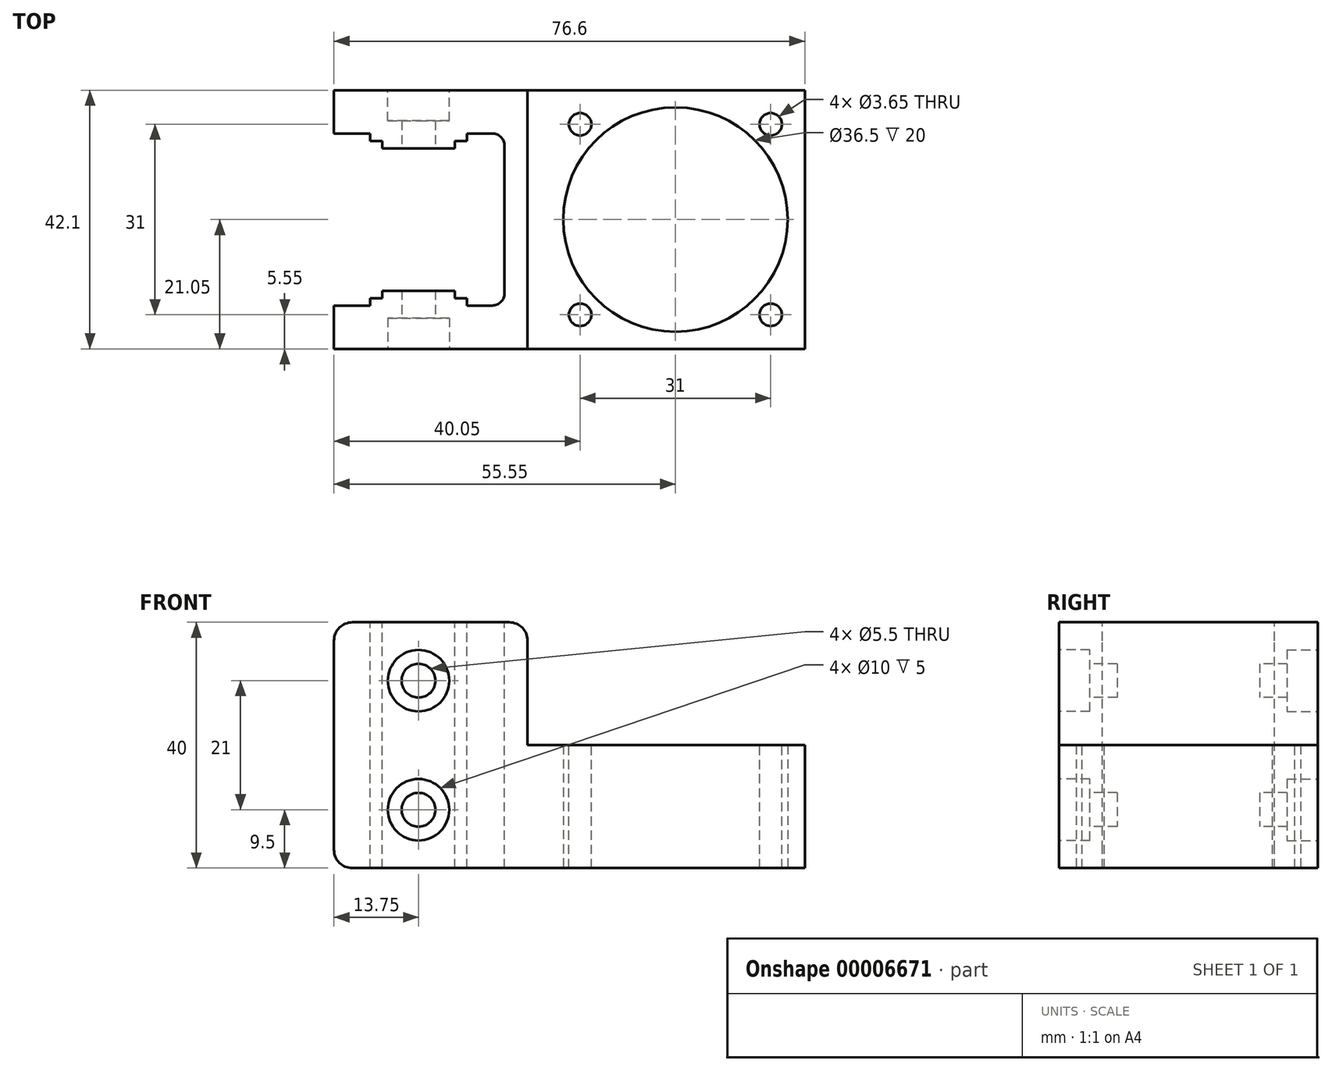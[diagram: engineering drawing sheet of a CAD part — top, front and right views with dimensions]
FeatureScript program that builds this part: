
annotation { "Feature Type Name" : "Feature", "Feature Type Description" : "" }
export const myFeature = defineFeature(function(context is Context, id is Id, definition is map)
    precondition{}
    {
        {
            var Q0;
            Q0=qCreatedBy(makeId("Top.planeOp"),FACE);
            var sketch = newSketch(context, id + "F0", { "sketchPlane" : qUnion([Q0])});
            skLineSegment(sketch, "E0.bottom", {"start": v(-34.5, 0) * mm, "end": v(42.1, 0) * mm});
            skLineSegment(sketch, "E0.top", {"start": v(-34.5, 42.1) * mm, "end": v(42.1, 42.1) * mm});
            skLineSegment(sketch, "E0.right", {"start": v(42.1, 0) * mm, "end": v(42.1, 42.1) * mm});
            skCircle(sketch, "E1", {"center": v(21.05, 21.05) * mm, "radius": 18.25 * mm});
            skLineSegment(sketch, "E2.0", {"start": v(-34.5, 0) * mm, "end": v(-34.5, 42.1) * mm});
            skSolve(sketch);
        }
        {
            var Q0;
            Q0 = qSketchRegion(id + "F0", true);
            extrude(context, id + "F1", {"entities" : qUnion([Q0]), "depth" : 20 * mm});
        }
        {
            var Q0;
            Q0=makeQuery(id+"F1.opExtrude","CAP_FACE",FACE,{"disambiguationData":[OSD([sQuery(id+"F0.wireOp",EDGE,"E0.bottom"),sQuery(id+"F0.wireOp",EDGE,"E0.top"),sQuery(id+"F0.wireOp",EDGE,"E0.right"),sQuery(id+"F0.wireOp",EDGE,"E1"),sQuery(id+"F0.wireOp",EDGE,"E2.0")])],"isStart":false});
            var sketch = newSketch(context, id + "F2", { "sketchPlane" : qUnion([Q0])});
            skLineSegment(sketch, "E3.0", {"start": v(21.05, 0) * mm, "end": v(21.05, 46.92) * mm, "construction": true});
            skLineSegment(sketch, "E4.0", {"start": v(0, 21.05) * mm, "end": v(47.18, 21.05) * mm, "construction": true});
            skLineSegment(sketch, "E5.0", {"start": v(36.55, 0) * mm, "end": v(36.55, 46.92) * mm, "construction": true});
            skLineSegment(sketch, "E6.0", {"start": v(5.55, 0) * mm, "end": v(5.55, 46.92) * mm, "construction": true});
            skLineSegment(sketch, "E7.0", {"start": v(0, 5.55) * mm, "end": v(47.18, 5.55) * mm, "construction": true});
            skLineSegment(sketch, "E8.0", {"start": v(0, 36.55) * mm, "end": v(47.18, 36.55) * mm, "construction": true});
            skCircle(sketch, "E9", {"center": v(5.55, 36.55) * mm, "radius": 1.82 * mm});
            skCircle(sketch, "E10", {"center": v(36.55, 36.55) * mm, "radius": 1.82 * mm});
            skCircle(sketch, "E11", {"center": v(36.55, 5.55) * mm, "radius": 1.82 * mm});
            skCircle(sketch, "E12", {"center": v(5.55, 5.55) * mm, "radius": 1.82 * mm});
            skSolve(sketch);
        }
        {
            var Q0;
            Q0 = qSketchRegion(id + "F2", true);
            extrude(context, id + "F3", {"entities" : qUnion([Q0]), "operationType" : NewBodyOperationType.REMOVE, "endBound" : BoundingType.THROUGH_ALL, "oppositeDirection" : true, "depth" : 25 * mm});
        }
        {
            var Q0;
            Q0=makeQuery(id+"F1.opExtrude","CAP_FACE",FACE,{"disambiguationData":[OSD([sQuery(id+"F0.wireOp",EDGE,"E0.bottom"),sQuery(id+"F0.wireOp",EDGE,"E0.top"),sQuery(id+"F0.wireOp",EDGE,"E0.right"),sQuery(id+"F0.wireOp",EDGE,"E1"),sQuery(id+"F0.wireOp",EDGE,"E2.0")])],"isStart":false});
            var sketch = newSketch(context, id + "F4", { "sketchPlane" : qUnion([Q0])});
            skLineSegment(sketch, "E13.bottom", {"start": v(-34.5, 42.1) * mm, "end": v(-3, 42.1) * mm});
            skLineSegment(sketch, "E13.top", {"start": v(-34.5, 0) * mm, "end": v(-3, 0) * mm});
            skLineSegment(sketch, "E13.left", {"start": v(-34.5, 42.1) * mm, "end": v(-34.5, 0) * mm});
            skLineSegment(sketch, "E13.right", {"start": v(-3, 42.1) * mm, "end": v(-3, 0) * mm});
            skSolve(sketch);
        }
        {
            var Q0;
            Q0 = qSketchRegion(id + "F4", true);
            extrude(context, id + "F5", {"entities" : qUnion([Q0]), "operationType" : NewBodyOperationType.ADD, "depth" : 20 * mm});
        }
        {
            var Q0;
            Q0=makeQuery(id+"F5.boolean.opBoolean","MERGE",FACE,{"derivedFrom":[makeQuery(id+"F1.opExtrude","SWEPT_FACE",FACE,{"disambiguationData":[OSD([sQuery(id+"F0.wireOp",EDGE,"E0.bottom")])]}),makeQuery(id+"F5.opExtrude","SWEPT_FACE",FACE,{"disambiguationData":[OSD([sQuery(id+"F4.wireOp",EDGE,"E13.top")])]})]});
            var sketch = newSketch(context, id + "F6", { "sketchPlane" : qUnion([Q0])});
            skLineSegment(sketch, "E14", {"start": v(-20.75, 40) * mm, "end": v(-20.75, 0) * mm, "construction": true});
            skLineSegment(sketch, "E15", {"start": v(-34.5, 0) * mm, "end": v(-10.11, 0) * mm, "construction": true});
            skLineSegment(sketch, "E16", {"start": v(-34.5, 40) * mm, "end": v(-8.27, 40) * mm, "construction": true});
            skLineSegment(sketch, "E17.0", {"start": v(-34.5, 30.5) * mm, "end": v(-8.27, 30.5) * mm, "construction": true});
            skLineSegment(sketch, "E18.0", {"start": v(-34.5, 9.5) * mm, "end": v(-10.11, 9.5) * mm, "construction": true});
            skCircle(sketch, "E19", {"center": v(-20.75, 30.5) * mm, "radius": 2.75 * mm});
            skCircle(sketch, "E20", {"center": v(-20.75, 9.5) * mm, "radius": 2.75 * mm});
            skSolve(sketch);
        }
        {
            var Q0;
            Q0 = qSketchRegion(id + "F6", true);
            extrude(context, id + "F7", {"entities" : qUnion([Q0]), "operationType" : NewBodyOperationType.REMOVE, "endBound" : BoundingType.THROUGH_ALL, "oppositeDirection" : true, "depth" : 25 * mm});
        }
        {
            var Q0;
            Q0=makeQuery(id+"F5.opExtrude","CAP_EDGE",EDGE,{"disambiguationData":[OSD([sQuery(id+"F4.wireOp",EDGE,"E13.left")])],"isStart":false});
            var Q1;
            Q1=makeQuery(id+"F5.opExtrude","CAP_EDGE",EDGE,{"disambiguationData":[OSD([sQuery(id+"F4.wireOp",EDGE,"E13.right")])],"isStart":false});
            var Q2;
            Q2=makeQuery(id+"F5.opExtrude","CAP_EDGE",EDGE,{"disambiguationData":[OSD([sQuery(id+"F4.wireOp",EDGE,"E13.right")])],"isStart":true});
            var Q3;
            Q3=makeQuery(id+"F1.opExtrude","CAP_EDGE",EDGE,{"disambiguationData":[OSD([sQuery(id+"F0.wireOp",EDGE,"E2.0")])],"isStart":true});
            fillet(context, id + "F8", {"entities" : qUnion([Q0, Q1, Q2, Q3]), "radius" : 3 * mm, "tangentPropagation" : true, "allowEdgeOverflow" : false});
        }
        {
            var Q0;
            Q0=makeQuery(id+"F5.boolean.opBoolean","MERGE",FACE,{"derivedFrom":[makeQuery(id+"F1.opExtrude","SWEPT_FACE",FACE,{"disambiguationData":[OSD([sQuery(id+"F0.wireOp",EDGE,"E0.bottom")])]}),makeQuery(id+"F5.opExtrude","SWEPT_FACE",FACE,{"disambiguationData":[OSD([sQuery(id+"F4.wireOp",EDGE,"E13.top")])]})]});
            var sketch = newSketch(context, id + "F9", { "sketchPlane" : qUnion([Q0])});
            skCircle(sketch, "E21", {"center": v(-20.75, 30.5) * mm, "radius": 5 * mm});
            skCircle(sketch, "E22", {"center": v(-20.75, 9.5) * mm, "radius": 5 * mm});
            skSolve(sketch);
        }
        {
            var Q0;
            Q0 = qSketchRegion(id + "F9", true);
            extrude(context, id + "F10", {"entities" : qUnion([Q0]), "operationType" : NewBodyOperationType.REMOVE, "oppositeDirection" : true, "depth" : 5 * mm});
        }
        {
            var Q0;
            Q0=makeQuery(id+"F5.boolean.opBoolean","MERGE",FACE,{"derivedFrom":[makeQuery(id+"F1.opExtrude","SWEPT_FACE",FACE,{"disambiguationData":[OSD([sQuery(id+"F0.wireOp",EDGE,"E0.top")])]}),makeQuery(id+"F5.opExtrude","SWEPT_FACE",FACE,{"disambiguationData":[OSD([sQuery(id+"F4.wireOp",EDGE,"E13.bottom")])]})]});
            var sketch = newSketch(context, id + "F11", { "sketchPlane" : qUnion([Q0])});
            skCircle(sketch, "E23", {"center": v(20.75, 30.5) * mm, "radius": 5 * mm});
            skCircle(sketch, "E24", {"center": v(20.75, 9.5) * mm, "radius": 5 * mm});
            skSolve(sketch);
        }
        {
            var Q0;
            Q0 = qSketchRegion(id + "F11", true);
            extrude(context, id + "F12", {"entities" : qUnion([Q0]), "operationType" : NewBodyOperationType.REMOVE, "oppositeDirection" : true, "depth" : 5 * mm});
        }
        {
            var Q0;
            Q0=makeQuery(id+"F5.opExtrude","CAP_FACE",FACE,{"disambiguationData":[OSD([sQuery(id+"F4.wireOp",EDGE,"E13.bottom"),sQuery(id+"F4.wireOp",EDGE,"E13.top"),sQuery(id+"F4.wireOp",EDGE,"E13.left"),sQuery(id+"F4.wireOp",EDGE,"E13.right")])],"isStart":false});
            var sketch = newSketch(context, id + "F13", { "sketchPlane" : qUnion([Q0])});
            skLineSegment(sketch, "E25.0", {"start": v(-14.85, 32.65) * mm, "end": v(-26.65, 32.65) * mm});
            skLineSegment(sketch, "E26.0", {"start": v(-26.65, 33.85) * mm, "end": v(-28.65, 33.85) * mm});
            skLineSegment(sketch, "E27.0", {"start": v(-12.85, 33.85) * mm, "end": v(-14.85, 33.85) * mm});
            skLineSegment(sketch, "E28.0", {"start": v(-8.75, 35.05) * mm, "end": v(-12.85, 35.05) * mm});
            skLineSegment(sketch, "E29.0", {"start": v(-28.65, 35.05) * mm, "end": v(-34.5, 35.05) * mm});
            skLineSegment(sketch, "E30.0", {"start": v(-28.65, 35.05) * mm, "end": v(-28.65, 33.85) * mm});
            skLineSegment(sketch, "E31.0", {"start": v(-26.65, 33.85) * mm, "end": v(-26.65, 32.65) * mm});
            skLineSegment(sketch, "E32.0", {"start": v(-14.85, 33.85) * mm, "end": v(-14.85, 32.65) * mm});
            skLineSegment(sketch, "E33.0", {"start": v(-12.85, 35.05) * mm, "end": v(-12.85, 33.85) * mm});
            skLineSegment(sketch, "E34.0", {"start": v(-6.75, 33.05) * mm, "end": v(-6.75, 9.05) * mm});
            skLineSegment(sketch, "E35.0", {"start": v(-28.65, 7.05) * mm, "end": v(-34.5, 7.05) * mm});
            skLineSegment(sketch, "E36.0", {"start": v(-26.65, 8.25) * mm, "end": v(-28.65, 8.25) * mm});
            skLineSegment(sketch, "E37.0", {"start": v(-28.65, 8.25) * mm, "end": v(-28.65, 7.05) * mm});
            skLineSegment(sketch, "E38.0", {"start": v(-26.65, 9.45) * mm, "end": v(-26.65, 8.25) * mm});
            skLineSegment(sketch, "E39.0", {"start": v(-14.85, 9.45) * mm, "end": v(-26.65, 9.45) * mm});
            skLineSegment(sketch, "E40.0", {"start": v(-14.85, 9.45) * mm, "end": v(-14.85, 8.25) * mm});
            skLineSegment(sketch, "E41.0", {"start": v(-12.85, 8.25) * mm, "end": v(-14.85, 8.25) * mm});
            skLineSegment(sketch, "E42.0", {"start": v(-12.85, 8.25) * mm, "end": v(-12.85, 7.05) * mm});
            skLineSegment(sketch, "E43.0", {"start": v(-8.75, 7.05) * mm, "end": v(-12.85, 7.05) * mm});
            skLineSegment(sketch, "E44", {"start": v(-34.5, 35.05) * mm, "end": v(-34.5, 7.05) * mm});
            skPoint(sketch, "E45.visualSharp", {"position": v(-6.75, 35.05) * mm});
            skArc(sketch, "E45.filletArc", {"start": v(-6.75, 33.05) * mm, "mid": v(-7.34, 34.46) * mm, "end": v(-8.75, 35.05) * mm});
            skPoint(sketch, "E46.visualSharp", {"position": v(-6.75, 7.05) * mm});
            skArc(sketch, "E46.filletArc", {"start": v(-8.75, 7.05) * mm, "mid": v(-7.34, 7.64) * mm, "end": v(-6.75, 9.05) * mm});
            skSolve(sketch);
        }
        {
            var Q0;
            Q0 = qSketchRegion(id + "F13", true);
            extrude(context, id + "F14", {"entities" : qUnion([Q0]), "operationType" : NewBodyOperationType.REMOVE, "endBound" : BoundingType.THROUGH_ALL, "oppositeDirection" : true, "depth" : 25 * mm});
        }
    });
